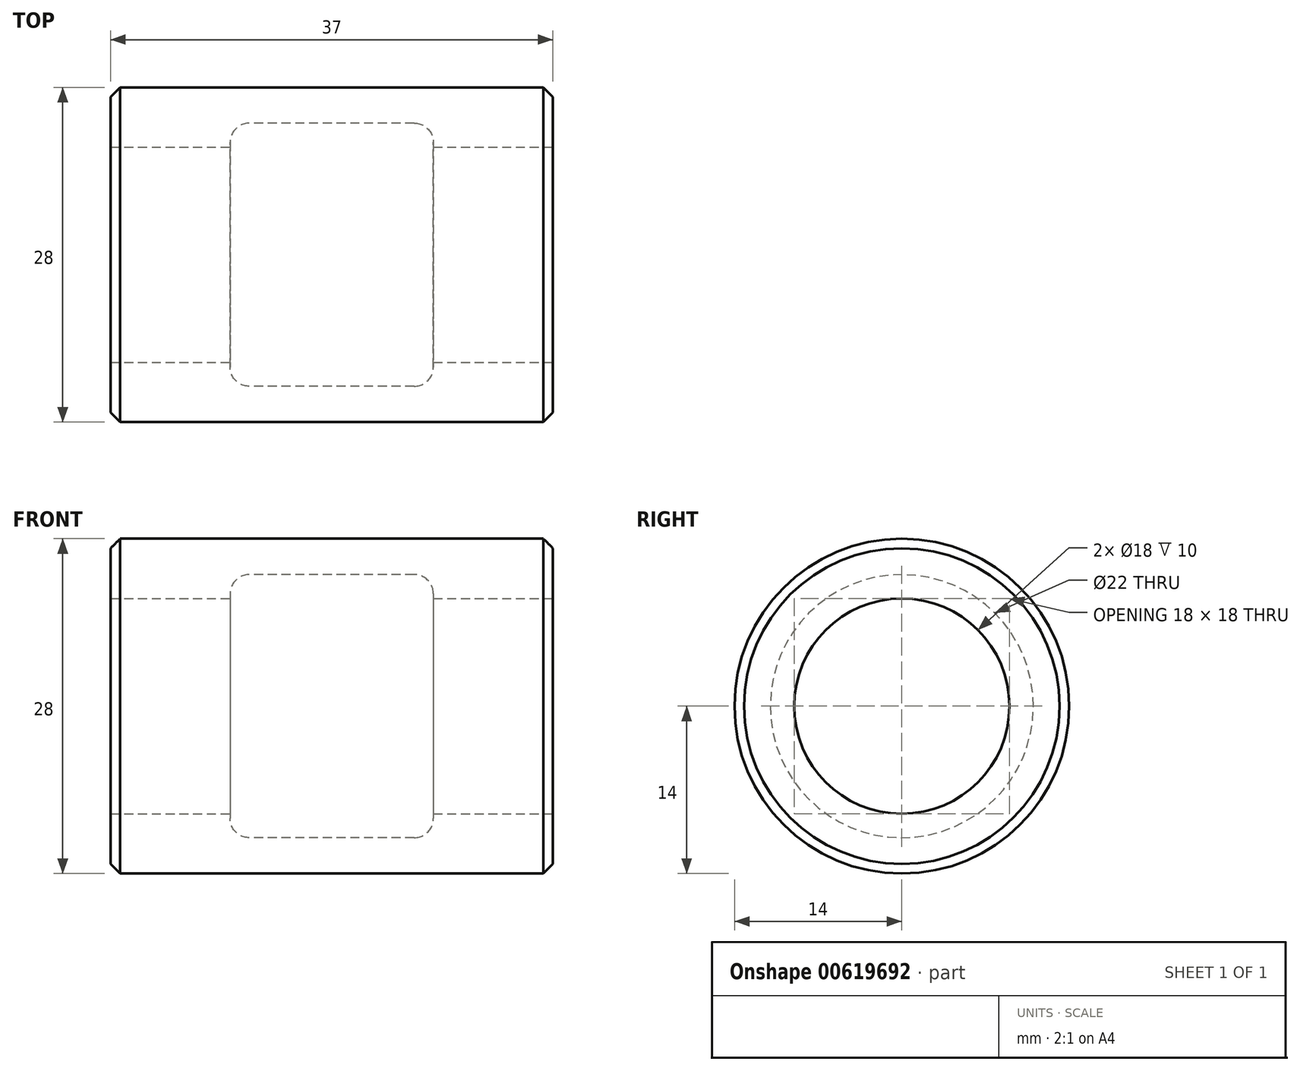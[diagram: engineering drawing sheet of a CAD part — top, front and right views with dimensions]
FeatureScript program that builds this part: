
annotation { "Feature Type Name" : "Feature", "Feature Type Description" : "" }
export const myFeature = defineFeature(function(context is Context, id is Id, definition is map)
    precondition{}
    {
        {
            var Q0;
            Q0=qCreatedBy(makeId("Front.planeOp"),FACE);
            var sketch = newSketch(context, id + "F0", { "sketchPlane" : qUnion([Q0])});
            skLineSegment(sketch, "E0.bottom", {"start": v(-27, -16.37) * mm, "end": v(-17, -16.37) * mm});
            skLineSegment(sketch, "E0.top", {"start": v(-27, -30.37) * mm, "end": v(10, -30.37) * mm});
            skLineSegment(sketch, "E0.left", {"start": v(-27, -16.37) * mm, "end": v(-27, -30.37) * mm});
            skLineSegment(sketch, "E0.right", {"start": v(10, -16.37) * mm, "end": v(10, -30.37) * mm});
            skLineSegment(sketch, "E1.top", {"start": v(-17, -27.37) * mm, "end": v(0, -27.37) * mm});
            skLineSegment(sketch, "E1.left", {"start": v(-17, -16.37) * mm, "end": v(-17, -27.37) * mm});
            skLineSegment(sketch, "E1.right", {"start": v(0, -16.37) * mm, "end": v(0, -27.37) * mm});
            skLineSegment(sketch, "E2", {"start": v(0, -16.37) * mm, "end": v(10, -16.37) * mm});
            skSolve(sketch);
        }
        {
            var Q0;
            Q0 = qSketchRegion(id + "F0", true);
            var Q1;
            Q1=sQuery(id+"F0.wireOp",EDGE,"E0.bottom");
            revolve(context, id + "F1", {"entities" : qUnion([Q0]), "axis" : qUnion([Q1]), "revolveType" : RevolveType.FULL});
        }
        {
            var Q0;
            Q0=makeQuery(id+"F1.opRevolve","SWEPT_FACE",FACE,{"disambiguationData":[OSD([sQuery(id+"F0.wireOp",EDGE,"E0.right")])]});
            var sketch = newSketch(context, id + "F2", { "sketchPlane" : qUnion([Q0])});
            skCircle(sketch, "E3", {"center": v(0, -16.37) * mm, "radius": 9 * mm});
            skSolve(sketch);
        }
        {
            var Q0;
            Q0 = qSketchRegion(id + "F2", true);
            extrude(context, id + "F3", {"entities" : qUnion([Q0]), "operationType" : NewBodyOperationType.REMOVE, "oppositeDirection" : true, "depth" : 37 * mm, "offsetDistance" : 25 * mm});
        }
        {
            var Q0;
            Q0=makeQuery(id+"F1.opRevolve","SWEPT_EDGE",EDGE,{"disambiguationData":[OSD([sQuery(id+"F0.wireOp",EDGE,"E0.top"),sQuery(id+"F0.wireOp",EDGE,"E0.right")])]});
            var Q1;
            Q1=makeQuery(id+"F1.opRevolve","SWEPT_EDGE",EDGE,{"disambiguationData":[OSD([sQuery(id+"F0.wireOp",EDGE,"E0.top"),sQuery(id+"F0.wireOp",EDGE,"E0.left")])]});
            chamfer(context, id + "F4", {"entities" : qUnion([Q0, Q1]), "width" : 0.8 * mm, "tangentPropagation" : true});
        }
        {
            var Q0;
            Q0=makeQuery(id+"F1.opRevolve","SWEPT_EDGE",EDGE,{"disambiguationData":[OSD([sQuery(id+"F0.wireOp",EDGE,"E1.top"),sQuery(id+"F0.wireOp",EDGE,"E1.left")])]});
            var Q1;
            Q1=makeQuery(id+"F1.opRevolve","SWEPT_EDGE",EDGE,{"disambiguationData":[OSD([sQuery(id+"F0.wireOp",EDGE,"E1.top"),sQuery(id+"F0.wireOp",EDGE,"E1.right")])]});
            fillet(context, id + "F5", {"entities" : qUnion([Q0, Q1]), "radius" : 1.6 * mm, "tangentPropagation" : true, "allowEdgeOverflow" : false});
        }
    });
